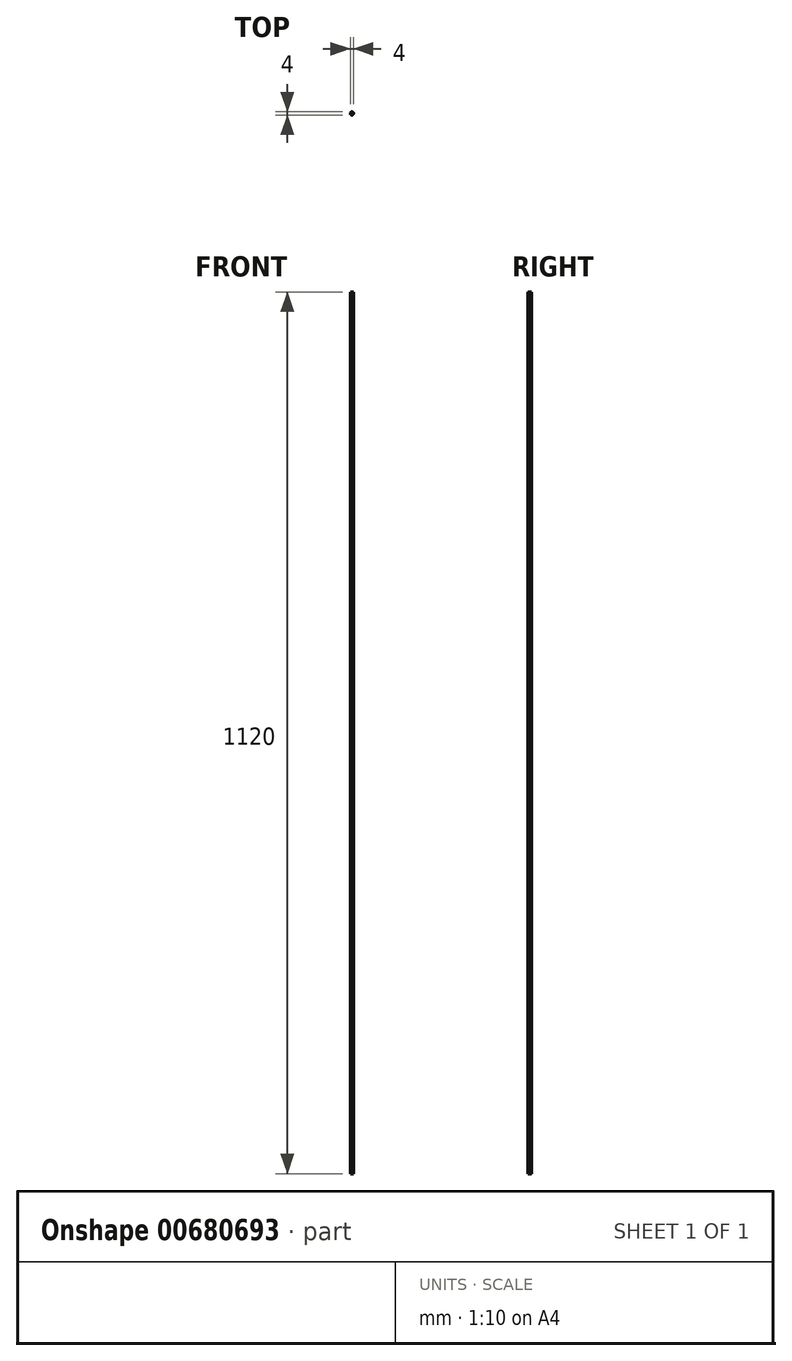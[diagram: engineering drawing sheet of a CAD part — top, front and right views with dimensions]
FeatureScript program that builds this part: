
annotation { "Feature Type Name" : "Feature", "Feature Type Description" : "" }
export const myFeature = defineFeature(function(context is Context, id is Id, definition is map)
    precondition{}
    {
        {
            var Q0;
            Q0=qCreatedBy(makeId("Top.planeOp"),FACE);
            var sketch = newSketch(context, id + "F0", { "sketchPlane" : qUnion([Q0])});
            skCircle(sketch, "E0", {"center": v(0, 0) * mm, "radius": 2 * mm});
            skSolve(sketch);
        }
        {
            var Q0;
            Q0=makeQuery(id+"F0.imprint","IMPRINT",FACE,{"disambiguationData":[TD([[makeQuery(id+"F0.imprint","IMPRINT",EDGE,{"derivedFrom":sQuery(id+"F0.wireOp",EDGE,"E0")}),1.0]])]});
            extrude(context, id + "F1", {"entities" : qUnion([Q0]), "depth" : 1120 * mm, "offsetDistance" : 25 * mm});
        }
    });
